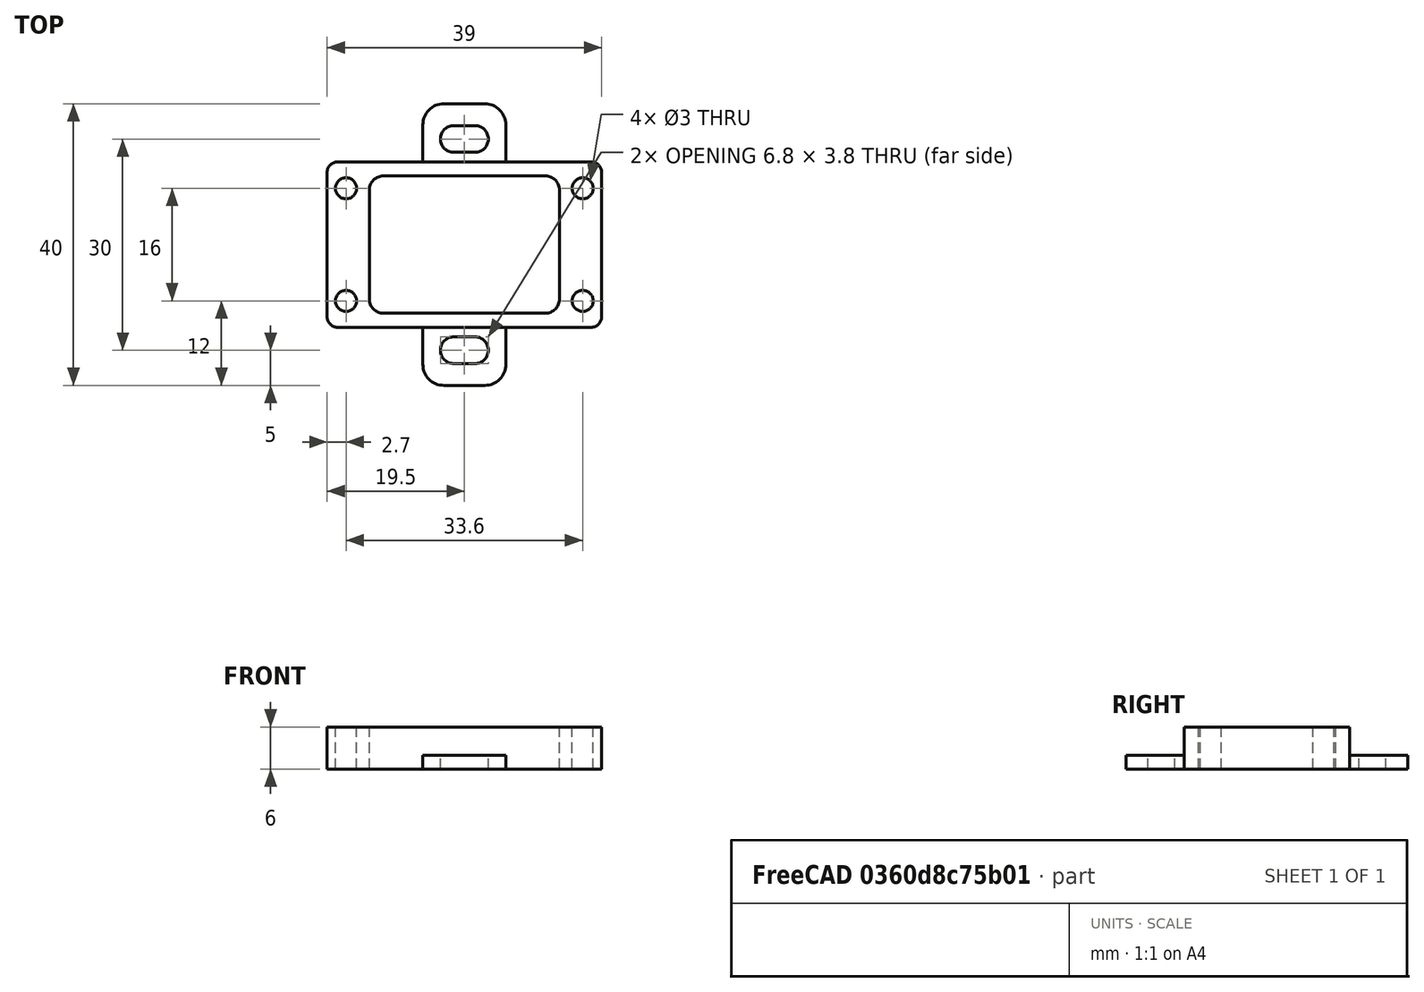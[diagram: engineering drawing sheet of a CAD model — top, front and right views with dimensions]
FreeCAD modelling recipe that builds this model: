
FCSTD DOCUMENT  (FreeCAD 0.19R23578 (Git))
Label: step_up_xl6009e1
License: All rights reserved
LicenseURL: http://en.wikipedia.org/wiki/All_rights_reserved
objects: Part::Box×2, Part::Fillet×2, Part::MultiFuse×2, Spreadsheet::Sheet×1, Part::Cylinder×1, Part::FeaturePython×1, Part::Feature×1, Part::Cut×1, App::Part×1
note: 10 computed .brp shape members not serialized (recipe doc carries the construction recipe); baked Part::Feature solids carry a one-line shape summary decoded from their .brp

FEATURE [Spreadsheet::Sheet] Spreadsheet  label="p"
  cells = A1=hole_x_dist; B1(hole_x_dist)=33.6; A2=hole_y_dist; B2(hole_y_dist)=16; A3=pcb_under; B3(pcb_under)=6; A4=pcb_x; B4(pcb_x)=39; A5=pcb_y; B5(pcb_y)=23.5; A6=hole_r; B6(hole_r)=1.5; A7=under_pcb_border_x; B7(under_pcb_border_x)=6; A8=under_pcb_border_y; B8(under_pcb_border_y)=2
FEATURE [Part::Box] Box  label="bottom cube"
  AttacherType = Attacher::AttachEngine3D
  Height = 6
  Length = 39
  Width = 23.5
  expr: Width = <<p>>.pcb_y
  expr: Length = <<p>>.pcb_x
  expr: Height = <<p>>.pcb_under
FEATURE [Part::Box] Box001  label="bottom extraction cube"
  AttacherType = Attacher::AttachEngine3D
  Height = 10
  Length = 27
  Placement = pos=(6,2,0) rot=(0,0,1;0rad)
  Width = 19.5
  expr: .Placement.Base.y = Spreadsheet.under_pcb_border_y
  expr: .Placement.Base.x = Spreadsheet.under_pcb_border_x
  expr: Length = <<p>>.pcb_x - <<p>>.under_pcb_border_x * 2
  expr: Width = <<p>>.pcb_y - <<p>>.under_pcb_border_y * 2
FEATURE [Part::Cylinder] Cylinder  label="pcb hole"
  Angle = 360
  AttacherType = Attacher::AttachEngine3D
  Height = 10
  Radius = 1.5
  expr: Radius = <<p>>.hole_r
FEATURE [Part::FeaturePython] Array001  label="hole array"  # Draft array (typed FeaturePython)
  Angle = 360
  ArrayType = 0
  Axis = (0,0,1)
  Base = -> Cylinder
  Center = (0,0,0)
  Fuse = false
  IntervalAxis = (0,0,0)
  IntervalX = (33.6,0,0)
  IntervalY = (0,16,0)
  IntervalZ = (0,0,1)
  NumberPolar = 1
  NumberX = 2
  NumberY = 2
  NumberZ = 1
  Placement = pos=(2.7,3.75,0) rot=(0,0,1;0rad)
  expr: .IntervalY.y = <<p>>.hole_y_dist
  expr: .IntervalX.x = <<p>>.hole_x_dist
  expr: .Placement.Base.x = (<<p>>.pcb_x - <<p>>.hole_x_dist) / 2
  expr: .Placement.Base.y = (<<p>>.pcb_y - <<p>>.hole_y_dist) / 2
FEATURE [Part::Fillet] Fillet001  label="bottom cube fillet"
  Base = -> Box
  Edges = 4 edges r=1.5: [Edge1,Edge3,Edge5,Edge7]
FEATURE [Part::Fillet] Fillet  label="bottom extraction cube fillet"
  Base = -> Box001
  Edges = 4 edges r=2: [Edge1,Edge3,Edge5,Edge7]
FEATURE [Part::MultiFuse] Fusion  label="bottom extraction"
  Shapes = -> [Array001,Fillet]
FEATURE [Part::Feature] Cut002002  label="attach plane y dir002"
  Placement = pos=(13.6,-8.25,0) rot=(0,0,1;0rad)
  shape: bbox 11.8 x 40 x 2 mm, 20 faces (baked)
FEATURE [Part::MultiFuse] Fusion002  label="bottom fusion"
  Shapes = -> [Fillet001,Cut002002]
FEATURE [Part::Cut] Cut  label="pcb box cut"
  Base = -> Fusion002
  Tool = -> Fusion
FEATURE [App::Part] Part  label="stepup_stepdown part"
  Group = -> [Cut]
  Origin = -> Origin
